# Revit family: Bidet_Seat-Elongated_Closed_Front-KOHLER-C3-150-K-8297T
name_source: partatom
category: Specialty Equipment
revit_build: Autodesk Revit 2017 (Build: 20160225_1515(x64)
units: mm (PartAtom-declared; Revit-internal decimal feet)

## family parameters
Cut with Voids When Loaded = No
Host = Face
OmniClass Number = 23.31.25.00
OmniClass Title = Toilet and Bath Specialties
Part Type = Normal
Room Calculation Point = No
Round Connector Dimension = Use Diameter
Shared = No

## types (1)
- 0-White
    ADA Compliant = No
    Apparent Load = 2200 VA
    Assembly Code = C1030200
    Date Modified = 12/30/2020
    Default Elevation = 0"
    Description = Qingshubao Smart Toilet Cover
    Electrical Connector = Yes
    Electrical Note = one dedicated circuit required
    Finish = Kohler-Plastic-0-White
    Height = 5 3/4"
    Length = 20 11/16"
    Manufacturer = KOHLER Co.
    Master Format 2014 = 10 28 00
    Master Format 2014 Name = Toilet, Bath, and Laundry Accessories
    Material = Plastic
    Model = K-8297T-0
    Product Documentation Link = https://files.kohler.com.cn
    Product Name = C3-150
    Product Page URL = https://www.kohler.com.cn
    Type = 1
    URL = http://www.kohler.com.cn
    Voltage = 220 V
    WaterSense Certified = No
    Width = 17 5/8"

## geometry (parser evidence)
native form markers: Sweep x4
no freeform markers — native parametric forms only
